# Revit family: NAU_Naughtone_Stng_Viv_Chair
name_source: partatom
category: Furniture
revit_build: Autodesk Revit 2015 (Build: 20140903_1530(x64)
units: mm (PartAtom-declared; Revit-internal decimal feet)

## types (5) — shared parameters
Additional Materials = Additional material and finish options available. Please contact Naughtone direct for further information.
Assembly Code = E2020200
AssetType = Movable
BIMObjectName = NAU_Naughtone_Seating_Viv_Chair
Base Options = Chromed mild steel base as standard. White powder coated steel frame and other RAL colours available on request. Please contact Naughtone direct for further information.
Category = Pr_40_50_12 : Chairs, seats and benches
Color = Various
DurationUnit = year
IfcExportAs = IfcFurnishingElementType
IfcExportType = CHAIR
Keynote = Pr_40_50_12
ManufacturerAddress = Knaresborough Tech Park, Manse Lane, Knaresborough, HG5 8LF
ManufacturerName = Naughtone
ManufacturerURL = www.naughtone.com
Material = Steel/Fabric
NBSDescription = Seating
NBSReference = 45-35-72/352
Name = Seating_Viv_Chair_Naughtone
ProductInformation = www.naughtone.com/products/viv/
Revision = 1
Shape = Rectangular
SustainabilityPerformance = FSC certified, FISP and ISO14001 certified
Uniclass2015Code = Pr_40_50_12
Uniclass2015Title = Chairs, seats and benches
Uniclass2015Version = Products v1.10
Version = 1
WarrantyDescription = Request warranty information from naughtone
WarrantyDurationLabor = 5
WarrantyDurationParts = 5
WarrantyDurationUnit = year
zero-valued in all types: Cost

## per-type parameters (varying)
| type | Description | Has4StarBase | Has5StarBase | HasSledBase | HasStarBase | IsArmchair | ModelReference | NominalHeight | NominalLength | NominalWidth | Size | Type Comments | URL |
| VIVCHSL | Viv Chair Sled Base | No | No | Yes | No | No | Viv Chair Sled Base | 780 mm  [stored 2.55906 ft] | 560 mm  [stored 1.83727 ft] | 515 mm  [stored 1.68963 ft] | 560 x 515 x 780mm | Stacking Chairs | http://www.naughtone.com |
| VIVACH4S | Viv Armchair 4 Star Base | Yes | No | No | Yes | Yes | Viv Armchair 4 Star Base | 785 mm | 530 mm  [stored 1.73885 ft] | 500 mm  [stored 1.64042 ft] | 530 x 500 x 785mm |  | www.naughtone.com |
| VIVCH4S | Viv 4 Star Base | Yes | No | No | Yes | No | Viv 4 Star Base | 785 mm | 530 mm  [stored 1.73885 ft] | 500 mm  [stored 1.64042 ft] | 530 x 500 x 785mm |  | http://www.naughtone.com |
| VIVACH5S | Viv Armchair 5 Star Base | No | Yes | No | Yes | Yes | Viv Armchair 5 Star Base | 785 mm | 530 mm  [stored 1.73885 ft] | 635 mm | 530 x 635 x 785mm |  | www.naughtone.com |
| VIVCH5S | Viv 5 Star Base | No | Yes | No | Yes | No | Viv 5 Star Base | 785 mm | 530 mm  [stored 1.73885 ft] | 635 mm | 530 x 635 x 785mm |  | www.naughtone.com |

note: column(s) folded — value = type name in every type: Model, ModelNumber

note: [stored X ft] marks values corroborated as IEEE doubles in the binary element streams (Revit-internal decimal feet)

## geometry (parser evidence)
native form markers: Sweep x3
no freeform markers — native parametric forms only
